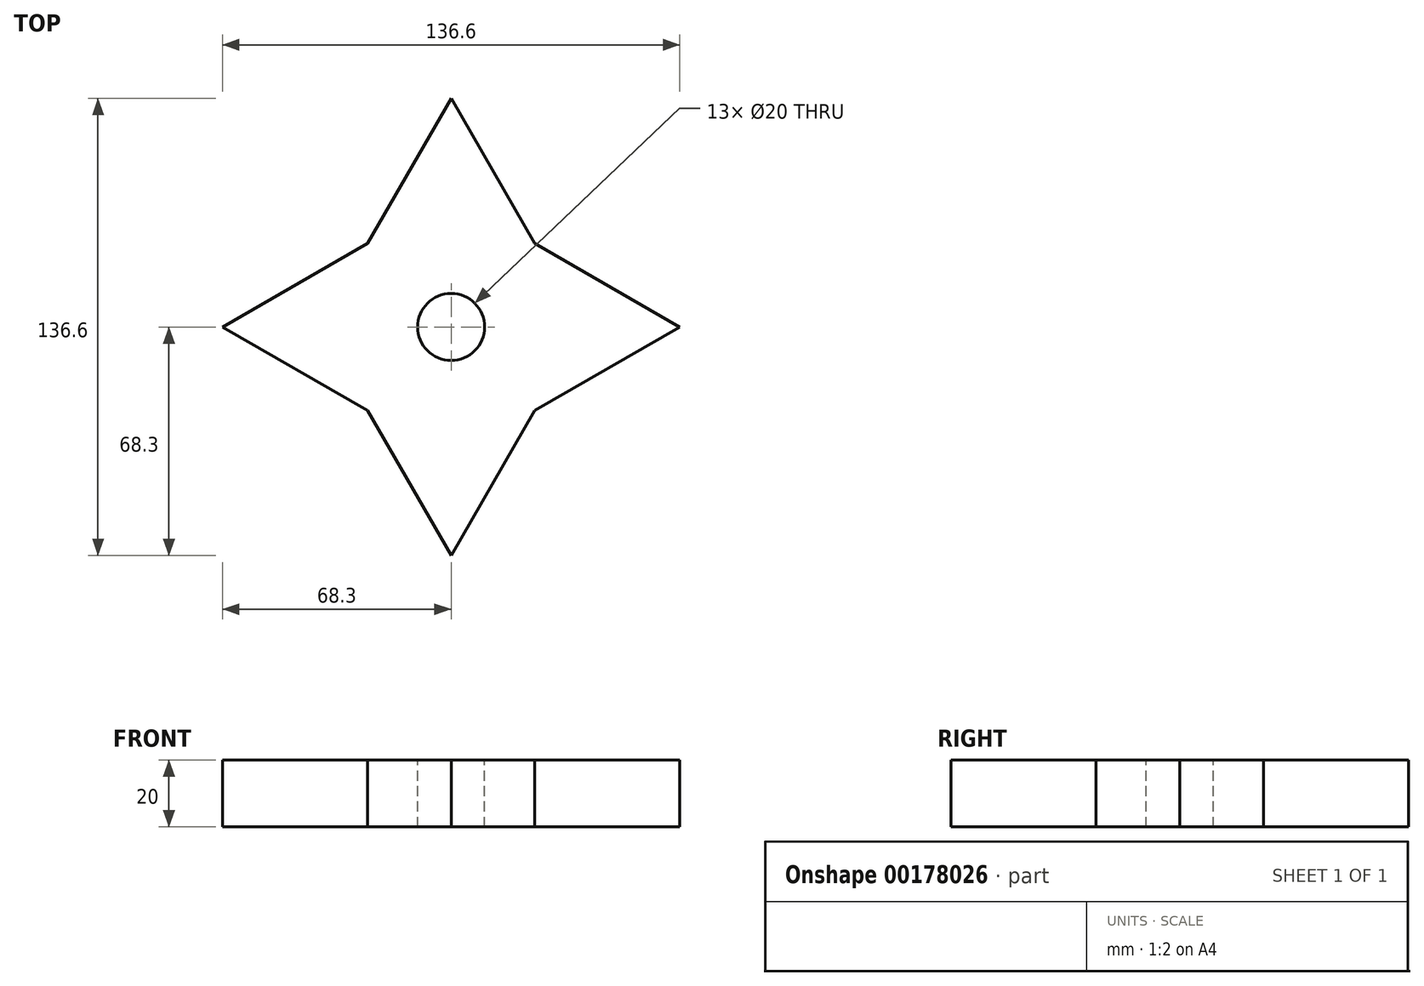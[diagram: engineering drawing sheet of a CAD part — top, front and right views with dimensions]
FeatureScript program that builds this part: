
annotation { "Feature Type Name" : "Feature", "Feature Type Description" : "" }
export const myFeature = defineFeature(function(context is Context, id is Id, definition is map)
    precondition{}
    {
        {
            var Q0;
            Q0=qCreatedBy(makeId("Top.planeOp"),FACE);
            var sketch = newSketch(context, id + "F0", { "sketchPlane" : qUnion([Q0])});
            skLineSegment(sketch, "E0.bottom", {"start": v(25, 25) * mm, "end": v(-25, 25) * mm});
            skLineSegment(sketch, "E0.top", {"start": v(25, -25) * mm, "end": v(-25, -25) * mm});
            skLineSegment(sketch, "E0.left", {"start": v(25, 25) * mm, "end": v(25, -25) * mm});
            skLineSegment(sketch, "E0.right", {"start": v(-25, 25) * mm, "end": v(-25, -25) * mm});
            skPoint(sketch, "E0.middle", {"position": v(0, 0) * mm});
            skLineSegment(sketch, "E1", {"start": v(0, 0) * mm, "end": v(0, 25) * mm, "construction": true});
            skLineSegment(sketch, "E2", {"start": v(-25, 25) * mm, "end": v(0, 68.3) * mm});
            skLineSegment(sketch, "E3.MirrorCS", {"start": v(25, 25) * mm, "end": v(0, 68.3) * mm});
            skLineSegment(sketch, "E4.1.0", {"start": v(-25, 25) * mm, "end": v(-68.3, 0) * mm});
            skLineSegment(sketch, "E4.1.1", {"start": v(-25, -25) * mm, "end": v(-68.3, 0) * mm});
            skLineSegment(sketch, "E4.2.0", {"start": v(-25, -25) * mm, "end": v(0, -68.3) * mm});
            skLineSegment(sketch, "E4.2.1", {"start": v(25, -25) * mm, "end": v(0, -68.3) * mm});
            skLineSegment(sketch, "E4.3.0", {"start": v(25, -25) * mm, "end": v(68.3, 0) * mm});
            skLineSegment(sketch, "E4.3.1", {"start": v(25, 25) * mm, "end": v(68.3, 0) * mm});
            skSolve(sketch);
        }
        {
            var Q0;
            Q0=qSketchRegion(id+"F0",true);
            extrude(context, id + "F1", {"entities" : qUnion([Q0]), "depth" : 10 * mm, "hasSecondDirection" : true, "secondDirectionOppositeDirection" : true, "secondDirectionDepth" : 10 * mm});
        }
        {
            var Q0;
            Q0=makeQuery(id+"F1.opExtrude","CAP_FACE",FACE,{"disambiguationData":[OSD([sQuery(id+"F0.wireOp",EDGE,"E2"),sQuery(id+"F0.wireOp",EDGE,"E3.MirrorCS"),sQuery(id+"F0.wireOp",EDGE,"E4.1.0"),sQuery(id+"F0.wireOp",EDGE,"E4.1.1"),sQuery(id+"F0.wireOp",EDGE,"E4.2.0"),sQuery(id+"F0.wireOp",EDGE,"E4.2.1"),sQuery(id+"F0.wireOp",EDGE,"E4.3.0"),sQuery(id+"F0.wireOp",EDGE,"E4.3.1")])],"isStart":false});
            var sketch = newSketch(context, id + "F2", { "sketchPlane" : qUnion([Q0])});
            skCircle(sketch, "E5", {"center": v(0, 0) * mm, "radius": 10 * mm});
            skSolve(sketch);
        }
        {
            var Q0;
            Q0=qSketchRegion(id+"F2",true);
            extrude(context, id + "F3", {"entities" : qUnion([Q0]), "operationType" : NewBodyOperationType.REMOVE, "endBound" : BoundingType.THROUGH_ALL, "oppositeDirection" : true, "depth" : 25 * mm});
        }
    });
